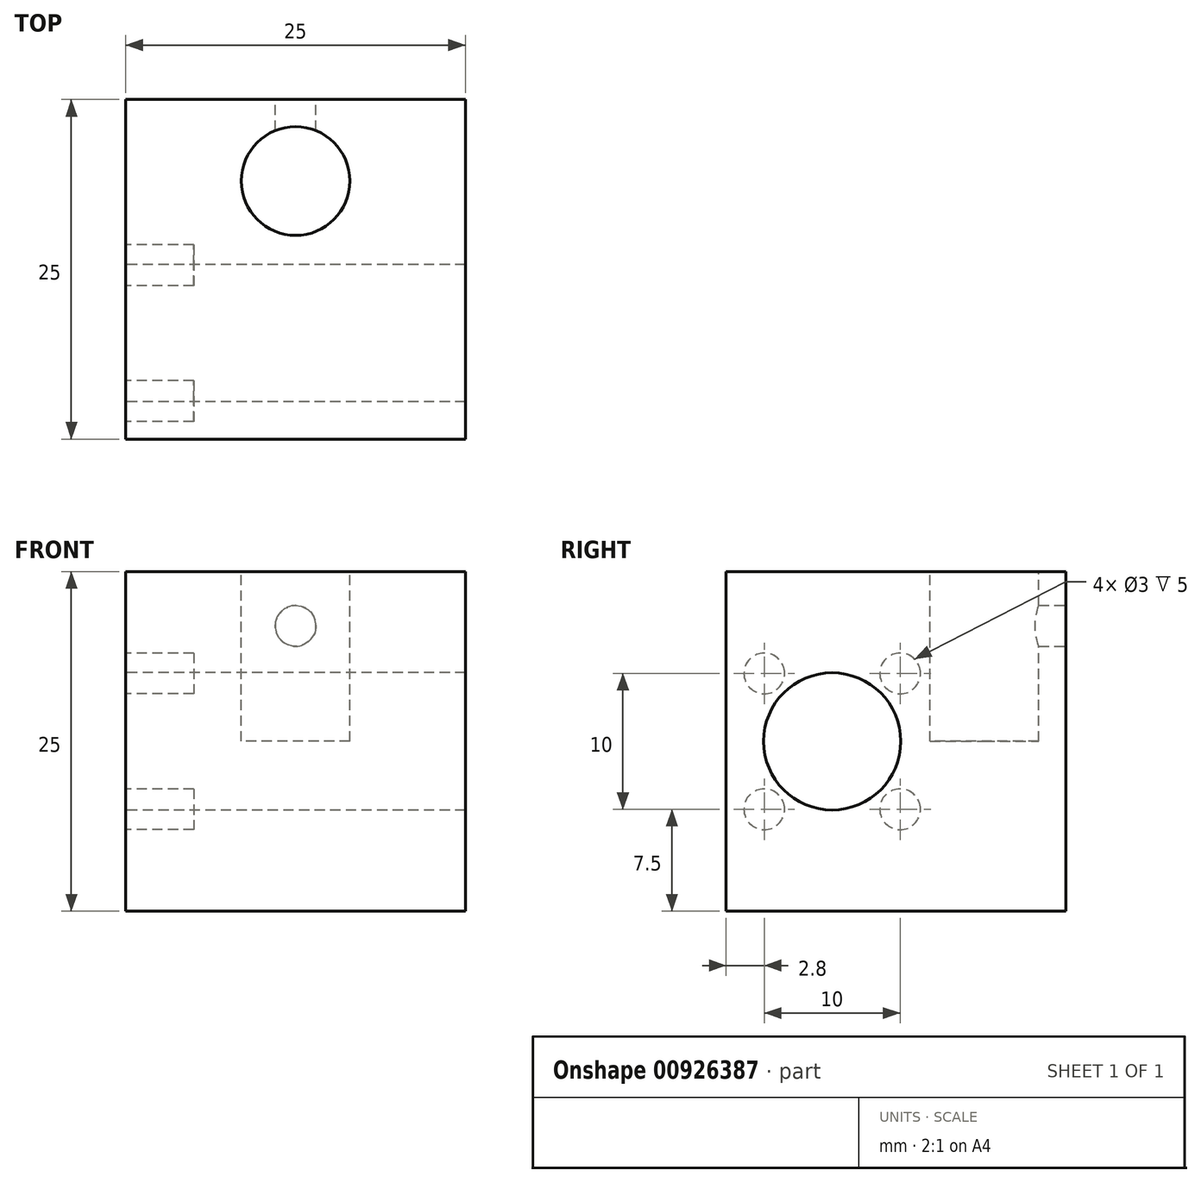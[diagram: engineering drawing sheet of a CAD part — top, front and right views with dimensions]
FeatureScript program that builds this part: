
annotation { "Feature Type Name" : "Feature", "Feature Type Description" : "" }
export const myFeature = defineFeature(function(context is Context, id is Id, definition is map)
    precondition{}
    {
        {
            var Q0;
            Q0=qCreatedBy(makeId("Top.planeOp"),FACE);
            var sketch = newSketch(context, id + "F0", { "sketchPlane" : qUnion([Q0])});
            skLineSegment(sketch, "E0.bottom", {"start": v(0, 0) * mm, "end": v(25, 0) * mm});
            skLineSegment(sketch, "E0.top", {"start": v(0, 25) * mm, "end": v(25, 25) * mm});
            skLineSegment(sketch, "E0.left", {"start": v(0, 0) * mm, "end": v(0, 25) * mm});
            skLineSegment(sketch, "E0.right", {"start": v(25, 0) * mm, "end": v(25, 25) * mm});
            skSolve(sketch);
        }
        {
            var Q0;
            Q0 = qSketchRegion(id + "F0", true);
            extrude(context, id + "F1", {"entities" : qUnion([Q0]), "depth" : 25 * mm, "offsetDistance" : 25 * mm});
        }
        {
            var Q0;
            Q0=makeQuery(id+"F1.opExtrude","CAP_FACE",FACE,{"disambiguationData":[OSD([sQuery(id+"F0.wireOp",EDGE,"E0.bottom"),sQuery(id+"F0.wireOp",EDGE,"E0.top"),sQuery(id+"F0.wireOp",EDGE,"E0.left"),sQuery(id+"F0.wireOp",EDGE,"E0.right")])],"isStart":false});
            var sketch = newSketch(context, id + "F2", { "sketchPlane" : qUnion([Q0])});
            skLineSegment(sketch, "E1", {"start": v(12.5, 25) * mm, "end": v(12.5, 0) * mm, "construction": true});
            skLineSegment(sketch, "E2", {"start": v(0, 19) * mm, "end": v(25, 19) * mm, "construction": true});
            skCircle(sketch, "E3", {"center": v(12.5, 19) * mm, "radius": 4 * mm});
            skSolve(sketch);
        }
        {
            var Q0;
            Q0 = qSketchRegion(id + "F2", true);
            extrude(context, id + "F3", {"entities" : qUnion([Q0]), "operationType" : NewBodyOperationType.REMOVE, "oppositeDirection" : true, "depth" : 12.5 * mm, "offsetDistance" : 25 * mm});
        }
        {
            var Q0;
            Q0=makeQuery(id+"F1.opExtrude","SWEPT_FACE",FACE,{"disambiguationData":[OSD([sQuery(id+"F0.wireOp",EDGE,"E0.top")])]});
            var sketch = newSketch(context, id + "F4", { "sketchPlane" : qUnion([Q0])});
            skLineSegment(sketch, "E4", {"start": v(-12.5, 0) * mm, "end": v(-12.5, 25) * mm, "construction": true});
            skLineSegment(sketch, "E5", {"start": v(0, 21) * mm, "end": v(-25, 21) * mm, "construction": true});
            skCircle(sketch, "E6", {"center": v(-12.5, 21) * mm, "radius": 1.5 * mm});
            skSolve(sketch);
        }
        {
            var Q0;
            Q0 = qSketchRegion(id + "F4", true);
            extrude(context, id + "F5", {"entities" : qUnion([Q0]), "operationType" : NewBodyOperationType.REMOVE, "oppositeDirection" : true, "depth" : 6 * mm, "offsetDistance" : 25 * mm});
        }
        {
            var Q0;
            Q0=makeQuery(id+"F1.opExtrude","SWEPT_FACE",FACE,{"disambiguationData":[OSD([sQuery(id+"F0.wireOp",EDGE,"E0.left")])]});
            var sketch = newSketch(context, id + "F6", { "sketchPlane" : qUnion([Q0])});
            skLineSegment(sketch, "E7", {"start": v(-25, 12.5) * mm, "end": v(0, 12.5) * mm, "construction": true});
            skLineSegment(sketch, "E8", {"start": v(-2.8, 0) * mm, "end": v(-2.8, 25) * mm, "construction": true});
            skLineSegment(sketch, "E9", {"start": v(-7.8, 0) * mm, "end": v(-7.8, 25) * mm, "construction": true});
            skLineSegment(sketch, "E10", {"start": v(-25, 7.5) * mm, "end": v(0, 7.5) * mm, "construction": true});
            skCircle(sketch, "E11", {"center": v(-2.8, 7.5) * mm, "radius": 1.5 * mm});
            skCircle(sketch, "E12.MirrorC", {"center": v(-2.8, 17.5) * mm, "radius": 1.5 * mm});
            skCircle(sketch, "E13.MirrorC", {"center": v(-12.8, 7.5) * mm, "radius": 1.5 * mm});
            skCircle(sketch, "E14.MirrorC", {"center": v(-12.8, 17.5) * mm, "radius": 1.5 * mm});
            skLineSegment(sketch, "E15.MirrorCS", {"start": v(-12.8, 0) * mm, "end": v(-12.8, 25) * mm, "construction": true});
            skLineSegment(sketch, "E16.MirrorCS", {"start": v(-25, 17.5) * mm, "end": v(0, 17.5) * mm, "construction": true});
            skSolve(sketch);
        }
        {
            var Q0;
            Q0 = qSketchRegion(id + "F6", true);
            extrude(context, id + "F7", {"entities" : qUnion([Q0]), "operationType" : NewBodyOperationType.REMOVE, "oppositeDirection" : true, "depth" : 5 * mm, "offsetDistance" : 25 * mm});
        }
        {
            var Q0;
            Q0=makeQuery(id+"F1.opExtrude","SWEPT_FACE",FACE,{"disambiguationData":[OSD([sQuery(id+"F0.wireOp",EDGE,"E0.left")])]});
            var sketch = newSketch(context, id + "F8", { "sketchPlane" : qUnion([Q0])});
            skLineSegment(sketch, "E17", {"start": v(-25, 12.5) * mm, "end": v(0, 12.5) * mm, "construction": true});
            skLineSegment(sketch, "E18", {"start": v(-7.8, 0) * mm, "end": v(-7.8, 25) * mm, "construction": true});
            skCircle(sketch, "E19", {"center": v(-7.8, 12.5) * mm, "radius": 5.05 * mm});
            skSolve(sketch);
        }
        {
            var Q0;
            Q0 = qSketchRegion(id + "F8", true);
            extrude(context, id + "F9", {"entities" : qUnion([Q0]), "operationType" : NewBodyOperationType.REMOVE, "endBound" : BoundingType.THROUGH_ALL, "oppositeDirection" : true, "depth" : 25 * mm, "offsetDistance" : 25 * mm});
        }
    });
